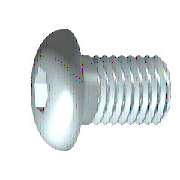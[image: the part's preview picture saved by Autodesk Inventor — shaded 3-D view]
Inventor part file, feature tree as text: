
AUTODESK INVENTOR PART (.ipt)
format: ipt  version: 2025 (Build 290162010, 162A)  size: 187,904 bytes
history: native  units: mm (DEFAULTED — no unit token found)
features: extrude x1, plane x1, fillet x1
ambient origin geometry x7: Origin, YZ Plane, XY Plane, X Axis, Y Axis, Z Axis, Center Point
bodies: Solid1 (feature_tree), Body (feature_tree)
feature tree (3):
  extrude  "Slot"  Depth=18.0mm
  plane  "Work Plane1"
  fillet  "Fillet2"  Radius=0.306825mm
